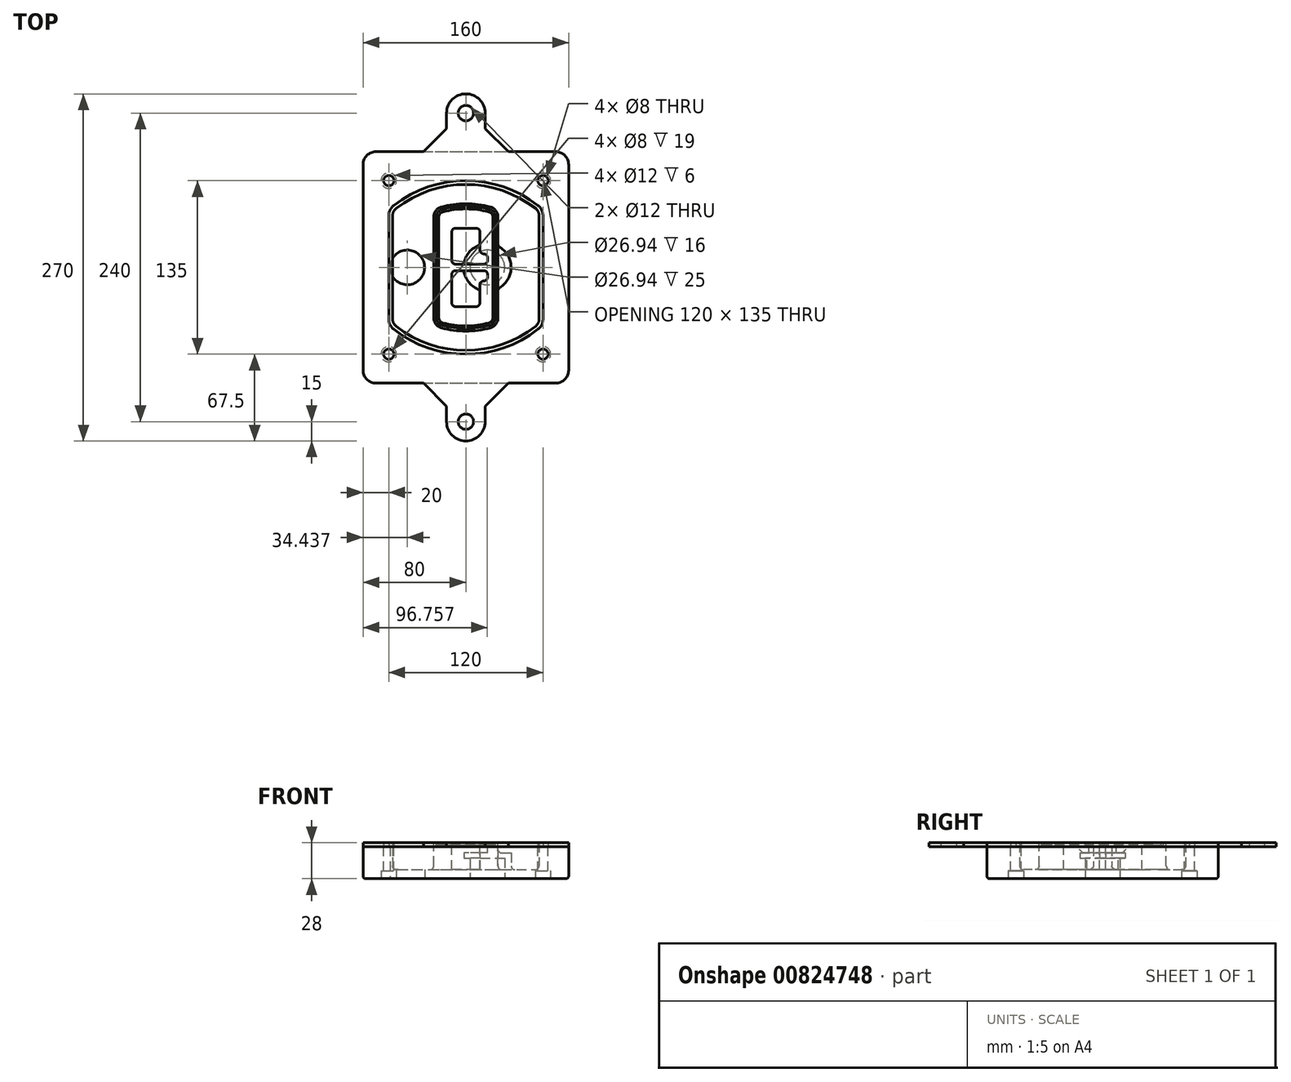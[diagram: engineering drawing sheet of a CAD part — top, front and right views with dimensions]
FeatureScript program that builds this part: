
annotation { "Feature Type Name" : "Feature", "Feature Type Description" : "" }
export const myFeature = defineFeature(function(context is Context, id is Id, definition is map)
    precondition{}
    {
        {
            var Q0;
            Q0=qCreatedBy(makeId("Top.planeOp"),FACE);
            var sketch = newSketch(context, id + "F0", { "sketchPlane" : qUnion([Q0])});
            skPoint(sketch, "E0.rect.middle", {"position": v(0, 0) * mm});
            skLineSegment(sketch, "E1.bottom", {"start": v(-70, -90) * mm, "end": v(70, -90) * mm});
            skLineSegment(sketch, "E1.top", {"start": v(-70, 90) * mm, "end": v(70, 90) * mm});
            skLineSegment(sketch, "E1.left", {"start": v(-80, -80) * mm, "end": v(-80, 80) * mm});
            skLineSegment(sketch, "E1.right", {"start": v(80, -80) * mm, "end": v(80, 80) * mm});
            skLineSegment(sketch, "E2", {"start": v(-80, 90) * mm, "end": v(80, -90) * mm, "construction": true});
            skLineSegment(sketch, "E3", {"start": v(80, 90) * mm, "end": v(-80, -90) * mm, "construction": true});
            skCircle(sketch, "E4", {"center": v(-60, 67.5) * mm, "radius": 4 * mm});
            skCircle(sketch, "E5", {"center": v(60, 67.5) * mm, "radius": 4 * mm});
            skCircle(sketch, "E6", {"center": v(60, -67.5) * mm, "radius": 4 * mm});
            skCircle(sketch, "E7", {"center": v(-60, -67.5) * mm, "radius": 4 * mm});
            skLineSegment(sketch, "E8", {"start": v(-60, 67.5) * mm, "end": v(60, 67.5) * mm, "construction": true});
            skLineSegment(sketch, "E9", {"start": v(60, 67.5) * mm, "end": v(60, -67.5) * mm, "construction": true});
            skLineSegment(sketch, "E10", {"start": v(60, -67.5) * mm, "end": v(-60, -67.5) * mm, "construction": true});
            skLineSegment(sketch, "E11", {"start": v(-60, -67.5) * mm, "end": v(-60, 67.5) * mm, "construction": true});
            skLineSegment(sketch, "E12", {"start": v(-60, 40.3) * mm, "end": v(-60, -40.3) * mm});
            skLineSegment(sketch, "E13", {"start": v(60, 40.3) * mm, "end": v(60, -40.3) * mm});
            skArc(sketch, "E14", {"start": v(56.15, 48.18) * mm, "mid": v(0, 67.5) * mm, "end": v(-56.15, 48.18) * mm});
            skArc(sketch, "E15", {"start": v(-56.15, -48.18) * mm, "mid": v(0, -67.5) * mm, "end": v(56.15, -48.18) * mm});
            skLineSegment(sketch, "E16", {"start": v(-60, 0) * mm, "end": v(60, 0) * mm, "construction": true});
            skPoint(sketch, "E17.visualSharp", {"position": v(-60, -45) * mm});
            skArc(sketch, "E17.filletArc", {"start": v(-60, -40.3) * mm, "mid": v(-58.99, -44.68) * mm, "end": v(-56.15, -48.18) * mm});
            skPoint(sketch, "E18.visualSharp", {"position": v(-60, 45) * mm});
            skArc(sketch, "E18.filletArc", {"start": v(-56.15, 48.18) * mm, "mid": v(-58.99, 44.68) * mm, "end": v(-60, 40.3) * mm});
            skPoint(sketch, "E19.visualSharp", {"position": v(60, 45) * mm});
            skArc(sketch, "E19.filletArc", {"start": v(60, 40.3) * mm, "mid": v(58.99, 44.68) * mm, "end": v(56.15, 48.18) * mm});
            skPoint(sketch, "E20.visualSharp", {"position": v(60, -45) * mm});
            skArc(sketch, "E20.filletArc", {"start": v(56.15, -48.18) * mm, "mid": v(58.99, -44.68) * mm, "end": v(60, -40.3) * mm});
            skPoint(sketch, "E21.visualSharp", {"position": v(-80, 90) * mm});
            skArc(sketch, "E21.filletArc", {"start": v(-70, 90) * mm, "mid": v(-77.07, 87.07) * mm, "end": v(-80, 80) * mm});
            skPoint(sketch, "E22.visualSharp", {"position": v(80, 90) * mm});
            skArc(sketch, "E22.filletArc", {"start": v(80, 80) * mm, "mid": v(77.07, 87.07) * mm, "end": v(70, 90) * mm});
            skPoint(sketch, "E23.visualSharp", {"position": v(80, -90) * mm});
            skArc(sketch, "E23.filletArc", {"start": v(70, -90) * mm, "mid": v(77.07, -87.07) * mm, "end": v(80, -80) * mm});
            skPoint(sketch, "E24.visualSharp", {"position": v(-80, -90) * mm});
            skArc(sketch, "E24.filletArc", {"start": v(-80, -80) * mm, "mid": v(-77.07, -87.07) * mm, "end": v(-70, -90) * mm});
            skArc(sketch, "E25.0", {"start": v(57, 40.3) * mm, "mid": v(56.3, 43.36) * mm, "end": v(54.3, 45.81) * mm});
            skLineSegment(sketch, "E25.1", {"start": v(57, 40.3) * mm, "end": v(57, -40.3) * mm});
            skArc(sketch, "E25.2", {"start": v(54.3, -45.81) * mm, "mid": v(56.3, -43.36) * mm, "end": v(57, -40.3) * mm});
            skArc(sketch, "E25.3", {"start": v(-54.3, -45.81) * mm, "mid": v(0, -64.5) * mm, "end": v(54.3, -45.81) * mm});
            skArc(sketch, "E25.4", {"start": v(-57, -40.3) * mm, "mid": v(-56.3, -43.36) * mm, "end": v(-54.3, -45.81) * mm});
            skArc(sketch, "E25.5", {"start": v(54.3, 45.81) * mm, "mid": v(0, 64.5) * mm, "end": v(-54.3, 45.81) * mm});
            skLineSegment(sketch, "E25.6", {"start": v(-57, 40.3) * mm, "end": v(-57, -40.3) * mm});
            skArc(sketch, "E25.7", {"start": v(-54.3, 45.81) * mm, "mid": v(-56.3, 43.36) * mm, "end": v(-57, 40.3) * mm});
            skArc(sketch, "E26.0", {"start": v(-58.62, 51.33) * mm, "mid": v(-62.58, 46.43) * mm, "end": v(-64, 40.3) * mm});
            skArc(sketch, "E26.1", {"start": v(58.62, 51.33) * mm, "mid": v(0, 71.5) * mm, "end": v(-58.62, 51.33) * mm});
            skArc(sketch, "E26.2", {"start": v(64, 40.3) * mm, "mid": v(62.58, 46.43) * mm, "end": v(58.62, 51.33) * mm});
            skLineSegment(sketch, "E26.3", {"start": v(64, 40.3) * mm, "end": v(64, -40.3) * mm});
            skArc(sketch, "E26.4", {"start": v(58.62, -51.33) * mm, "mid": v(62.58, -46.43) * mm, "end": v(64, -40.3) * mm});
            skLineSegment(sketch, "E26.5", {"start": v(-64, 40.3) * mm, "end": v(-64, -40.3) * mm});
            skArc(sketch, "E26.6", {"start": v(-58.62, -51.33) * mm, "mid": v(0, -71.5) * mm, "end": v(58.62, -51.33) * mm});
            skArc(sketch, "E26.7", {"start": v(-64, -40.3) * mm, "mid": v(-62.58, -46.43) * mm, "end": v(-58.62, -51.33) * mm});
            skSolve(sketch);
        }
        {
            var Q0;
            Q0=makeQuery(id+"F0.imprint","IMPRINT",FACE,{"disambiguationData":[TD([[makeQuery(id+"F0.imprint","IMPRINT",EDGE,{"derivedFrom":sQuery(id+"F0.wireOp",EDGE,"E1.bottom")}),1.0]])]});
            var Q1;
            Q1=makeQuery(id+"F0.imprint","IMPRINT",FACE,{"disambiguationData":[TD([[makeQuery(id+"F0.imprint","IMPRINT",EDGE,{"derivedFrom":sQuery(id+"F0.wireOp",EDGE,"E12")}),1.0]])]});
            var Q2;
            Q2=makeQuery(id+"F0.imprint","IMPRINT",FACE,{"disambiguationData":[TD([[makeQuery(id+"F0.imprint","IMPRINT",EDGE,{"derivedFrom":sQuery(id+"F0.wireOp",EDGE,"E25.0")}),1.0]])]});
            var Q3;
            Q3=makeQuery(id+"F0.imprint","IMPRINT",FACE,{"disambiguationData":[TD([[makeQuery(id+"F0.imprint","IMPRINT",EDGE,{"derivedFrom":sQuery(id+"F0.wireOp",EDGE,"E12")}),-1.0]])]});
            extrude(context, id + "F1", {"entities" : qUnion([Q0, Q1, Q2, Q3]), "oppositeDirection" : true, "depth" : 25 * mm});
        }
        {
            var Q0;
            Q0=makeQuery(id+"F0.imprint","IMPRINT",FACE,{"disambiguationData":[TD([[makeQuery(id+"F0.imprint","IMPRINT",EDGE,{"derivedFrom":sQuery(id+"F0.wireOp",EDGE,"E12")}),1.0]])]});
            extrude(context, id + "F2", {"entities" : qUnion([Q0]), "operationType" : NewBodyOperationType.ADD, "depth" : 3 * mm});
        }
        {
            var Q0;
            Q0=makeQuery(id+"F0.imprint","IMPRINT",FACE,{"disambiguationData":[TD([[makeQuery(id+"F0.imprint","IMPRINT",EDGE,{"derivedFrom":sQuery(id+"F0.wireOp",EDGE,"E25.0")}),1.0]])]});
            extrude(context, id + "F3", {"entities" : qUnion([Q0]), "operationType" : NewBodyOperationType.REMOVE, "oppositeDirection" : true, "depth" : 18 * mm});
        }
        {
            var Q0;
            Q0=makeQuery(id+"F2.opExtrude","CAP_FACE",FACE,{"disambiguationData":[OSD([sQuery(id+"F0.wireOp",EDGE,"E12"),sQuery(id+"F0.wireOp",EDGE,"E13"),sQuery(id+"F0.wireOp",EDGE,"E14"),sQuery(id+"F0.wireOp",EDGE,"E15"),sQuery(id+"F0.wireOp",EDGE,"E17.filletArc"),sQuery(id+"F0.wireOp",EDGE,"E18.filletArc"),sQuery(id+"F0.wireOp",EDGE,"E19.filletArc"),sQuery(id+"F0.wireOp",EDGE,"E20.filletArc"),sQuery(id+"F0.wireOp",EDGE,"E25.0"),sQuery(id+"F0.wireOp",EDGE,"E25.1"),sQuery(id+"F0.wireOp",EDGE,"E25.2"),sQuery(id+"F0.wireOp",EDGE,"E25.3"),sQuery(id+"F0.wireOp",EDGE,"E25.4"),sQuery(id+"F0.wireOp",EDGE,"E25.5"),sQuery(id+"F0.wireOp",EDGE,"E25.6"),sQuery(id+"F0.wireOp",EDGE,"E25.7")])],"isStart":false});
            var sketch = newSketch(context, id + "F4", { "sketchPlane" : qUnion([Q0])});
            skArc(sketch, "E27.0", {"start": v(-19.08, -46.97) * mm, "mid": v(0, -49.5) * mm, "end": v(19.08, -46.97) * mm});
            skArc(sketch, "E28.0", {"start": v(19.08, 46.97) * mm, "mid": v(0, 49.5) * mm, "end": v(-19.08, 46.97) * mm});
            skLineSegment(sketch, "E29", {"start": v(-25, 39.25) * mm, "end": v(-25, -39.25) * mm});
            skLineSegment(sketch, "E30", {"start": v(25, 39.25) * mm, "end": v(25, -39.25) * mm});
            skLineSegment(sketch, "E31", {"start": v(-25, 45.1) * mm, "end": v(25, 45.1) * mm, "construction": true});
            skLineSegment(sketch, "E32", {"start": v(-25, -45.1) * mm, "end": v(25, -45.1) * mm, "construction": true});
            skPoint(sketch, "E33.visualSharp", {"position": v(-25, 45.1) * mm});
            skArc(sketch, "E33.filletArc", {"start": v(-19.08, 46.97) * mm, "mid": v(-23.35, 44.11) * mm, "end": v(-25, 39.25) * mm});
            skPoint(sketch, "E34.visualSharp", {"position": v(25, 45.1) * mm});
            skArc(sketch, "E34.filletArc", {"start": v(25, 39.25) * mm, "mid": v(23.35, 44.11) * mm, "end": v(19.08, 46.97) * mm});
            skPoint(sketch, "E35.visualSharp", {"position": v(25, -45.1) * mm});
            skArc(sketch, "E35.filletArc", {"start": v(19.08, -46.97) * mm, "mid": v(23.35, -44.11) * mm, "end": v(25, -39.25) * mm});
            skPoint(sketch, "E36.visualSharp", {"position": v(-25, -45.1) * mm});
            skArc(sketch, "E36.filletArc", {"start": v(-25, -39.25) * mm, "mid": v(-23.35, -44.11) * mm, "end": v(-19.08, -46.97) * mm});
            skArc(sketch, "E37.0", {"start": v(54.3, 45.81) * mm, "mid": v(0, 64.5) * mm, "end": v(-54.3, 45.81) * mm});
            skArc(sketch, "E37.1", {"start": v(-54.3, 45.81) * mm, "mid": v(-56.3, 43.36) * mm, "end": v(-57, 40.3) * mm});
            skLineSegment(sketch, "E37.2", {"start": v(-57, 40.3) * mm, "end": v(-57, -40.3) * mm});
            skArc(sketch, "E37.3", {"start": v(-57, -40.3) * mm, "mid": v(-56.3, -43.36) * mm, "end": v(-54.3, -45.81) * mm});
            skArc(sketch, "E37.4", {"start": v(-54.3, -45.81) * mm, "mid": v(0, -64.5) * mm, "end": v(54.3, -45.81) * mm});
            skArc(sketch, "E37.5", {"start": v(54.3, -45.81) * mm, "mid": v(56.3, -43.36) * mm, "end": v(57, -40.3) * mm});
            skLineSegment(sketch, "E37.6", {"start": v(57, 40.3) * mm, "end": v(57, -40.3) * mm});
            skArc(sketch, "E37.7", {"start": v(57, 40.3) * mm, "mid": v(56.3, 43.36) * mm, "end": v(54.3, 45.81) * mm});
            skLineSegment(sketch, "E38.0", {"start": v(23, 39.25) * mm, "end": v(23, -39.25) * mm});
            skArc(sketch, "E38.1", {"start": v(18.56, -45.04) * mm, "mid": v(21.76, -42.9) * mm, "end": v(23, -39.25) * mm});
            skArc(sketch, "E38.2", {"start": v(-18.56, -45.04) * mm, "mid": v(0, -47.5) * mm, "end": v(18.56, -45.04) * mm});
            skArc(sketch, "E38.3", {"start": v(-23, -39.25) * mm, "mid": v(-21.76, -42.9) * mm, "end": v(-18.56, -45.04) * mm});
            skLineSegment(sketch, "E38.4", {"start": v(-23, 39.25) * mm, "end": v(-23, -39.25) * mm});
            skArc(sketch, "E38.5", {"start": v(23, 39.25) * mm, "mid": v(21.76, 42.9) * mm, "end": v(18.56, 45.04) * mm});
            skArc(sketch, "E38.6", {"start": v(-18.56, 45.04) * mm, "mid": v(-21.76, 42.9) * mm, "end": v(-23, 39.25) * mm});
            skArc(sketch, "E38.7", {"start": v(18.56, 45.04) * mm, "mid": v(0, 47.5) * mm, "end": v(-18.56, 45.04) * mm});
            skArc(sketch, "E39.0", {"start": v(21, 39.25) * mm, "mid": v(20.18, 41.68) * mm, "end": v(18.04, 43.1) * mm});
            skLineSegment(sketch, "E39.1", {"start": v(21, 39.25) * mm, "end": v(21, -39.25) * mm});
            skArc(sketch, "E39.2", {"start": v(18.04, -43.1) * mm, "mid": v(20.18, -41.68) * mm, "end": v(21, -39.25) * mm});
            skArc(sketch, "E39.3", {"start": v(-18.04, -43.1) * mm, "mid": v(0, -45.5) * mm, "end": v(18.04, -43.1) * mm});
            skArc(sketch, "E39.4", {"start": v(-21, -39.25) * mm, "mid": v(-20.18, -41.68) * mm, "end": v(-18.04, -43.1) * mm});
            skArc(sketch, "E39.5", {"start": v(18.04, 43.1) * mm, "mid": v(0, 45.5) * mm, "end": v(-18.04, 43.1) * mm});
            skLineSegment(sketch, "E39.6", {"start": v(-21, 39.25) * mm, "end": v(-21, -39.25) * mm});
            skArc(sketch, "E39.7", {"start": v(-18.04, 43.1) * mm, "mid": v(-20.18, 41.68) * mm, "end": v(-21, 39.25) * mm});
            skLineSegment(sketch, "E40", {"start": v(-25, 0) * mm, "end": v(25, 0) * mm, "construction": true});
            skLineSegment(sketch, "E41", {"start": v(-11, 5.5) * mm, "end": v(-11, 27.5) * mm});
            skLineSegment(sketch, "E42", {"start": v(-8, 30.5) * mm, "end": v(8, 30.5) * mm});
            skLineSegment(sketch, "E43", {"start": v(11, 27.5) * mm, "end": v(11, 13.5) * mm});
            skLineSegment(sketch, "E44", {"start": v(14, 10.5) * mm, "end": v(14, 10.5) * mm});
            skLineSegment(sketch, "E45", {"start": v(17, 7.5) * mm, "end": v(17, 5.5) * mm});
            skLineSegment(sketch, "E46", {"start": v(14, 2.5) * mm, "end": v(-8, 2.5) * mm});
            skPoint(sketch, "E47.visualSharp", {"position": v(-11, 30.5) * mm});
            skArc(sketch, "E47.filletArc", {"start": v(-8, 30.5) * mm, "mid": v(-10.12, 29.62) * mm, "end": v(-11, 27.5) * mm});
            skPoint(sketch, "E48.visualSharp", {"position": v(11, 30.5) * mm});
            skArc(sketch, "E48.filletArc", {"start": v(11, 27.5) * mm, "mid": v(10.12, 29.62) * mm, "end": v(8, 30.5) * mm});
            skPoint(sketch, "E49.visualSharp", {"position": v(11, 10.5) * mm});
            skArc(sketch, "E49.filletArc", {"start": v(11, 13.5) * mm, "mid": v(11.88, 11.38) * mm, "end": v(14, 10.5) * mm});
            skPoint(sketch, "E50.visualSharp", {"position": v(17, 10.5) * mm});
            skArc(sketch, "E50.filletArc", {"start": v(17, 7.5) * mm, "mid": v(16.12, 9.62) * mm, "end": v(14, 10.5) * mm});
            skPoint(sketch, "E51.visualSharp", {"position": v(17, 2.5) * mm});
            skArc(sketch, "E51.filletArc", {"start": v(14, 2.5) * mm, "mid": v(16.12, 3.38) * mm, "end": v(17, 5.5) * mm});
            skPoint(sketch, "E52.visualSharp", {"position": v(-11, 2.5) * mm});
            skArc(sketch, "E52.filletArc", {"start": v(-11, 5.5) * mm, "mid": v(-10.12, 3.38) * mm, "end": v(-8, 2.5) * mm});
            skLineSegment(sketch, "E53.0.MirrorCS", {"start": v(14, -2.5) * mm, "end": v(-8, -2.5) * mm});
            skArc(sketch, "E54.0.MirrorCS", {"start": v(-11, -5.5) * mm, "mid": v(-10.12, -3.38) * mm, "end": v(-8, -2.5) * mm});
            skLineSegment(sketch, "E55.0.MirrorCS", {"start": v(-11, -5.5) * mm, "end": v(-11, -27.5) * mm});
            skArc(sketch, "E56.0.MirrorCS", {"start": v(-8, -30.5) * mm, "mid": v(-10.12, -29.62) * mm, "end": v(-11, -27.5) * mm});
            skLineSegment(sketch, "E57.0.MirrorCS", {"start": v(-8, -30.5) * mm, "end": v(8, -30.5) * mm});
            skArc(sketch, "E58.0.MirrorCS", {"start": v(11, -27.5) * mm, "mid": v(10.12, -29.62) * mm, "end": v(8, -30.5) * mm});
            skLineSegment(sketch, "E59.0.MirrorCS", {"start": v(11, -27.5) * mm, "end": v(11, -13.5) * mm});
            skArc(sketch, "E60.0.MirrorCS", {"start": v(11, -13.5) * mm, "mid": v(11.88, -11.38) * mm, "end": v(14, -10.5) * mm});
            skArc(sketch, "E61.0.MirrorCS", {"start": v(17, -7.5) * mm, "mid": v(16.12, -9.62) * mm, "end": v(14, -10.5) * mm});
            skLineSegment(sketch, "E62.0.MirrorCS", {"start": v(17, -7.5) * mm, "end": v(17, -5.5) * mm});
            skArc(sketch, "E63.0.MirrorCS", {"start": v(14, -2.5) * mm, "mid": v(16.12, -3.38) * mm, "end": v(17, -5.5) * mm});
            skSolve(sketch);
        }
        {
            var Q0;
            Q0=makeQuery(id+"F4.imprint","IMPRINT",FACE,{"disambiguationData":[TD([[makeQuery(id+"F4.imprint","IMPRINT",EDGE,{"derivedFrom":sQuery(id+"F4.wireOp",EDGE,"E27.0")}),1.0]])]});
            var Q1;
            Q1=makeQuery(id+"F4.imprint","IMPRINT",FACE,{"disambiguationData":[TD([[makeQuery(id+"F4.imprint","IMPRINT",EDGE,{"derivedFrom":sQuery(id+"F4.wireOp",EDGE,"E38.0")}),-1.0]])]});
            var Q2;
            Q2=makeQuery(id+"F4.imprint","IMPRINT",FACE,{"disambiguationData":[TD([[makeQuery(id+"F4.imprint","IMPRINT",EDGE,{"derivedFrom":sQuery(id+"F4.wireOp",EDGE,"E39.0")}),1.0]])]});
            extrude(context, id + "F5", {"entities" : qUnion([Q0, Q1, Q2]), "operationType" : NewBodyOperationType.ADD, "endBound" : BoundingType.UP_TO_NEXT, "oppositeDirection" : true, "depth" : 25 * mm});
        }
        {
            var Q0;
            Q0=makeQuery(id+"F4.imprint","IMPRINT",FACE,{"disambiguationData":[TD([[makeQuery(id+"F4.imprint","IMPRINT",EDGE,{"derivedFrom":sQuery(id+"F4.wireOp",EDGE,"E38.0")}),-1.0]])]});
            extrude(context, id + "F6", {"entities" : qUnion([Q0]), "operationType" : NewBodyOperationType.REMOVE, "oppositeDirection" : true, "depth" : 2 * mm});
        }
        {
            var Q0;
            Q0=makeQuery(id+"F1.opExtrude","CAP_FACE",FACE,{"disambiguationData":[OSD([sQuery(id+"F0.wireOp",EDGE,"E1.bottom"),sQuery(id+"F0.wireOp",EDGE,"E1.top"),sQuery(id+"F0.wireOp",EDGE,"E1.left"),sQuery(id+"F0.wireOp",EDGE,"E1.right"),sQuery(id+"F0.wireOp",EDGE,"E4"),sQuery(id+"F0.wireOp",EDGE,"E5"),sQuery(id+"F0.wireOp",EDGE,"E6"),sQuery(id+"F0.wireOp",EDGE,"E7"),sQuery(id+"F0.wireOp",EDGE,"E21.filletArc"),sQuery(id+"F0.wireOp",EDGE,"E22.filletArc"),sQuery(id+"F0.wireOp",EDGE,"E23.filletArc"),sQuery(id+"F0.wireOp",EDGE,"E24.filletArc")])],"isStart":false});
            var sketch = newSketch(context, id + "F7", { "sketchPlane" : qUnion([Q0])});
            skCircle(sketch, "E64", {"center": v(16.76, 0) * mm, "radius": 13.47 * mm});
            skCircle(sketch, "E65", {"center": v(-45.56, 0) * mm, "radius": 13.47 * mm});
            skLineSegment(sketch, "E66", {"start": v(80, 0) * mm, "end": v(-80, 0) * mm});
            skCircle(sketch, "E67", {"center": v(16.76, 0) * mm, "radius": 18.47 * mm});
            skCircle(sketch, "E68", {"center": v(60, -67.5) * mm, "radius": 6 * mm});
            skCircle(sketch, "E69", {"center": v(-60, -67.5) * mm, "radius": 6 * mm});
            skCircle(sketch, "E70", {"center": v(-60, 67.5) * mm, "radius": 6 * mm});
            skCircle(sketch, "E71", {"center": v(60, 67.5) * mm, "radius": 6 * mm});
            skSolve(sketch);
        }
        {
            var Q0;
            {var subQ1=sQuery(id+"F7.wireOp",EDGE,"E66");var subQ4=sQuery(id+"F7.wireOp",EDGE,"E64");var subQ6=makeQuery(id+"F7.imprint","INTERSECT",VERTEX,{"disambiguationData":[OD(0.0)],"derivedFrom":[subQ4,subQ1]});Q0=makeQuery(id+"F7.imprint","IMPRINT",FACE,{"disambiguationData":[TD([[makeQuery(id+"F7.imprint","IMPRINT",EDGE,{"disambiguationData":[TD([[subQ6,-1.0]])],"derivedFrom":subQ4}),-1.0]])]});}
            var Q1;
            {var subQ0=sQuery(id+"F7.wireOp",EDGE,"E66");var subQ1=sQuery(id+"F7.wireOp",EDGE,"E64");var subQ3=makeQuery(id+"F7.imprint","INTERSECT",VERTEX,{"disambiguationData":[OD(0.0)],"derivedFrom":[subQ1,subQ0]});Q1=makeQuery(id+"F7.imprint","IMPRINT",FACE,{"disambiguationData":[TD([[makeQuery(id+"F7.imprint","IMPRINT",EDGE,{"disambiguationData":[TD([[subQ3,-1.0]])],"derivedFrom":subQ1}),1.0]])]});}
            var Q2;
            {var subQ0=sQuery(id+"F7.wireOp",EDGE,"E66");var subQ1=sQuery(id+"F7.wireOp",EDGE,"E64");var subQ3=makeQuery(id+"F7.imprint","INTERSECT",VERTEX,{"disambiguationData":[OD(0.0)],"derivedFrom":[subQ1,subQ0]});Q2=makeQuery(id+"F7.imprint","IMPRINT",FACE,{"disambiguationData":[TD([[makeQuery(id+"F7.imprint","IMPRINT",EDGE,{"disambiguationData":[TD([[subQ3,1.0]])],"derivedFrom":subQ1}),1.0]])]});}
            var Q3;
            {var subQ1=sQuery(id+"F7.wireOp",EDGE,"E66");var subQ4=sQuery(id+"F7.wireOp",EDGE,"E64");var subQ6=makeQuery(id+"F7.imprint","INTERSECT",VERTEX,{"disambiguationData":[OD(0.0)],"derivedFrom":[subQ4,subQ1]});Q3=makeQuery(id+"F7.imprint","IMPRINT",FACE,{"disambiguationData":[TD([[makeQuery(id+"F7.imprint","IMPRINT",EDGE,{"disambiguationData":[TD([[subQ6,1.0]])],"derivedFrom":subQ4}),-1.0]])]});}
            extrude(context, id + "F8", {"entities" : qUnion([Q0, Q1, Q2, Q3]), "operationType" : NewBodyOperationType.ADD, "oppositeDirection" : true, "depth" : 20 * mm});
        }
        {
            var Q0;
            {var subQ0=sQuery(id+"F7.wireOp",EDGE,"E66");var subQ1=sQuery(id+"F7.wireOp",EDGE,"E64");var subQ3=makeQuery(id+"F7.imprint","INTERSECT",VERTEX,{"disambiguationData":[OD(0.0)],"derivedFrom":[subQ1,subQ0]});Q0=makeQuery(id+"F7.imprint","IMPRINT",FACE,{"disambiguationData":[TD([[makeQuery(id+"F7.imprint","IMPRINT",EDGE,{"disambiguationData":[TD([[subQ3,-1.0]])],"derivedFrom":subQ1}),1.0]])]});}
            var Q1;
            {var subQ0=sQuery(id+"F7.wireOp",EDGE,"E66");var subQ1=sQuery(id+"F7.wireOp",EDGE,"E64");var subQ3=makeQuery(id+"F7.imprint","INTERSECT",VERTEX,{"disambiguationData":[OD(0.0)],"derivedFrom":[subQ1,subQ0]});Q1=makeQuery(id+"F7.imprint","IMPRINT",FACE,{"disambiguationData":[TD([[makeQuery(id+"F7.imprint","IMPRINT",EDGE,{"disambiguationData":[TD([[subQ3,1.0]])],"derivedFrom":subQ1}),1.0]])]});}
            extrude(context, id + "F9", {"entities" : qUnion([Q0, Q1]), "operationType" : NewBodyOperationType.REMOVE, "oppositeDirection" : true, "depth" : 16 * mm});
        }
        {
            var Q0;
            {var subQ0=sQuery(id+"F7.wireOp",EDGE,"E66");var subQ1=sQuery(id+"F7.wireOp",EDGE,"E65");var subQ3=makeQuery(id+"F7.imprint","INTERSECT",VERTEX,{"disambiguationData":[OD(0.0)],"derivedFrom":[subQ1,subQ0]});Q0=makeQuery(id+"F7.imprint","IMPRINT",FACE,{"disambiguationData":[TD([[makeQuery(id+"F7.imprint","IMPRINT",EDGE,{"disambiguationData":[TD([[subQ3,-1.0]])],"derivedFrom":subQ1}),1.0]])]});}
            var Q1;
            {var subQ0=sQuery(id+"F7.wireOp",EDGE,"E66");var subQ1=sQuery(id+"F7.wireOp",EDGE,"E65");var subQ3=makeQuery(id+"F7.imprint","INTERSECT",VERTEX,{"disambiguationData":[OD(0.0)],"derivedFrom":[subQ1,subQ0]});Q1=makeQuery(id+"F7.imprint","IMPRINT",FACE,{"disambiguationData":[TD([[makeQuery(id+"F7.imprint","IMPRINT",EDGE,{"disambiguationData":[TD([[subQ3,1.0]])],"derivedFrom":subQ1}),1.0]])]});}
            extrude(context, id + "F10", {"entities" : qUnion([Q0, Q1]), "operationType" : NewBodyOperationType.REMOVE, "oppositeDirection" : true, "depth" : 25 * mm});
        }
        {
            var Q0;
            Q0=makeQuery(id+"F7.imprint","IMPRINT",FACE,{"disambiguationData":[TD([[makeQuery(id+"F7.imprint","IMPRINT",EDGE,{"derivedFrom":sQuery(id+"F7.wireOp",EDGE,"E68")}),1.0]])]});
            var Q1;
            Q1=makeQuery(id+"F7.imprint","IMPRINT",FACE,{"disambiguationData":[TD([[makeQuery(id+"F7.imprint","IMPRINT",EDGE,{"derivedFrom":makeQuery(id+"F1.opExtrude","CAP_EDGE",EDGE,{"disambiguationData":[OSD([sQuery(id+"F0.wireOp",EDGE,"E5")])],"isStart":false})}),-1.0]])]});
            var Q2;
            Q2=makeQuery(id+"F7.imprint","IMPRINT",FACE,{"disambiguationData":[TD([[makeQuery(id+"F7.imprint","IMPRINT",EDGE,{"derivedFrom":sQuery(id+"F7.wireOp",EDGE,"E69")}),1.0]])]});
            var Q3;
            Q3=makeQuery(id+"F7.imprint","IMPRINT",FACE,{"disambiguationData":[TD([[makeQuery(id+"F7.imprint","IMPRINT",EDGE,{"derivedFrom":makeQuery(id+"F1.opExtrude","CAP_EDGE",EDGE,{"disambiguationData":[OSD([sQuery(id+"F0.wireOp",EDGE,"E4")])],"isStart":false})}),-1.0]])]});
            var Q4;
            Q4=makeQuery(id+"F7.imprint","IMPRINT",FACE,{"disambiguationData":[TD([[makeQuery(id+"F7.imprint","IMPRINT",EDGE,{"derivedFrom":sQuery(id+"F7.wireOp",EDGE,"E70")}),1.0]])]});
            var Q5;
            Q5=makeQuery(id+"F7.imprint","IMPRINT",FACE,{"disambiguationData":[TD([[makeQuery(id+"F7.imprint","IMPRINT",EDGE,{"derivedFrom":makeQuery(id+"F1.opExtrude","CAP_EDGE",EDGE,{"disambiguationData":[OSD([sQuery(id+"F0.wireOp",EDGE,"E7")])],"isStart":false})}),-1.0]])]});
            var Q6;
            Q6=makeQuery(id+"F7.imprint","IMPRINT",FACE,{"disambiguationData":[TD([[makeQuery(id+"F7.imprint","IMPRINT",EDGE,{"derivedFrom":sQuery(id+"F7.wireOp",EDGE,"E71")}),1.0]])]});
            var Q7;
            Q7=makeQuery(id+"F7.imprint","IMPRINT",FACE,{"disambiguationData":[TD([[makeQuery(id+"F7.imprint","IMPRINT",EDGE,{"derivedFrom":makeQuery(id+"F1.opExtrude","CAP_EDGE",EDGE,{"disambiguationData":[OSD([sQuery(id+"F0.wireOp",EDGE,"E6")])],"isStart":false})}),-1.0]])]});
            extrude(context, id + "F11", {"entities" : qUnion([Q0, Q1, Q2, Q3, Q4, Q5, Q6, Q7]), "operationType" : NewBodyOperationType.REMOVE, "oppositeDirection" : true, "depth" : 6 * mm});
        }
        {
            var Q0;
            Q0=makeQuery(id+"F9.boolean.opBoolean","COPY",FACE,{"derivedFrom":makeQuery(id+"F9.opExtrude","CAP_FACE",FACE,{"disambiguationData":[OSD([sQuery(id+"F7.wireOp",EDGE,"E64")])],"isStart":false})});
            var sketch = newSketch(context, id + "F12", { "sketchPlane" : qUnion([Q0])});
            skArc(sketch, "E72.0", {"start": v(11, 17.55) * mm, "mid": v(2.57, 11.82) * mm, "end": v(-1.54, 2.5) * mm});
            skArc(sketch, "E72.1", {"start": v(-1.54, -2.5) * mm, "mid": v(2.57, -11.82) * mm, "end": v(11, -17.55) * mm});
            skLineSegment(sketch, "E73", {"start": v(-1.54, -2.5) * mm, "end": v(14, -2.5) * mm});
            skLineSegment(sketch, "E74.0", {"start": v(14, 2.5) * mm, "end": v(-1.54, 2.5) * mm});
            skArc(sketch, "E74.1", {"start": v(14, 2.5) * mm, "mid": v(16.12, 3.38) * mm, "end": v(17, 5.5) * mm});
            skLineSegment(sketch, "E74.2", {"start": v(17, 7.5) * mm, "end": v(17, 5.5) * mm});
            skArc(sketch, "E74.3", {"start": v(17, 7.5) * mm, "mid": v(16.12, 9.62) * mm, "end": v(14, 10.5) * mm});
            skArc(sketch, "E74.4", {"start": v(11, 13.5) * mm, "mid": v(11.88, 11.38) * mm, "end": v(14, 10.5) * mm});
            skLineSegment(sketch, "E74.5", {"start": v(11, 17.55) * mm, "end": v(11, 13.5) * mm});
            skLineSegment(sketch, "E74.7", {"start": v(14, -2.5) * mm, "end": v(-1.54, -2.5) * mm});
            skArc(sketch, "E74.8", {"start": v(14, -2.5) * mm, "mid": v(16.12, -3.38) * mm, "end": v(17, -5.5) * mm});
            skLineSegment(sketch, "E74.9", {"start": v(17, -7.5) * mm, "end": v(17, -5.5) * mm});
            skArc(sketch, "E74.10", {"start": v(17, -7.5) * mm, "mid": v(16.12, -9.62) * mm, "end": v(14, -10.5) * mm});
            skArc(sketch, "E74.11", {"start": v(11, -13.5) * mm, "mid": v(11.88, -11.38) * mm, "end": v(14, -10.5) * mm});
            skLineSegment(sketch, "E74.12", {"start": v(11, -17.55) * mm, "end": v(11, -13.5) * mm});
            skPoint(sketch, "E75.orphan", {"position": v(11, -27.5) * mm});
            skPoint(sketch, "E76.orphan", {"position": v(-8, -2.5) * mm});
            skPoint(sketch, "E77.orphan", {"position": v(-8, 2.5) * mm});
            skPoint(sketch, "E78.orphan", {"position": v(11, 27.5) * mm});
            skSolve(sketch);
        }
        {
            var Q0;
            {var subQ7=sQuery(id+"F12.wireOp",EDGE,"E72.0");var subQ14=sQuery(id+"F12.wireOp",EDGE,"E72.1");var subQ16=sQuery(id+"F12.wireOp",EDGE,"E74.1");var subQ18=sQuery(id+"F12.wireOp",EDGE,"E74.8");Q0=qUnion([makeQuery(id+"F12.imprint","IMPRINT",FACE,{"disambiguationData":[TD([[makeQuery(id+"F12.imprint","IMPRINT",EDGE,{"derivedFrom":subQ7}),1.0]])]}),makeQuery(id+"F12.imprint","IMPRINT",FACE,{"disambiguationData":[TD([[makeQuery(id+"F12.imprint","IMPRINT",EDGE,{"derivedFrom":subQ14}),1.0]])]}),makeQuery(id+"F12.imprint","IMPRINT",FACE,{"disambiguationData":[TD([[makeQuery(id+"F12.imprint","IMPRINT",EDGE,{"derivedFrom":subQ16}),1.0]])]}),makeQuery(id+"F12.imprint","IMPRINT",FACE,{"disambiguationData":[TD([[makeQuery(id+"F12.imprint","IMPRINT",EDGE,{"derivedFrom":subQ18}),-1.0]])]})]);}
            var Q1;
            Q1=makeQuery(id+"F5.boolean.opBoolean","SPLIT",FACE,{"disambiguationData":[TD([makeQuery(id+"F5.opExtrude","SWEPT_FACE",FACE,{"disambiguationData":[OSD([sQuery(id+"F4.wireOp",EDGE,"E41")])]})])],"derivedFrom":makeQuery(id+"F3.boolean.opBoolean","COPY",FACE,{"derivedFrom":makeQuery(id+"F3.opExtrude","CAP_FACE",FACE,{"disambiguationData":[OSD([sQuery(id+"F0.wireOp",EDGE,"E25.0"),sQuery(id+"F0.wireOp",EDGE,"E25.1"),sQuery(id+"F0.wireOp",EDGE,"E25.2"),sQuery(id+"F0.wireOp",EDGE,"E25.3"),sQuery(id+"F0.wireOp",EDGE,"E25.4"),sQuery(id+"F0.wireOp",EDGE,"E25.5"),sQuery(id+"F0.wireOp",EDGE,"E25.6"),sQuery(id+"F0.wireOp",EDGE,"E25.7")])],"isStart":false})})});
            extrude(context, id + "F13", {"entities" : qUnion([Q0]), "operationType" : NewBodyOperationType.REMOVE, "endBound" : BoundingType.UP_TO_SURFACE, "endBoundEntityFace" : qUnion([Q1]), "depth" : 25 * mm});
        }
        {
            var Q0;
            Q0=makeQuery(id+"F3.boolean.opBoolean","COPY",EDGE,{"derivedFrom":makeQuery(id+"F3.opExtrude","CAP_EDGE",EDGE,{"disambiguationData":[OSD([sQuery(id+"F0.wireOp",EDGE,"E25.6")])],"isStart":false})});
            var Q1;
            Q1=makeQuery(id+"F8.boolean.opBoolean","INTERSECT",EDGE,{"derivedFrom":[makeQuery(id+"F5.opExtrude","SWEPT_FACE",FACE,{"disambiguationData":[OSD([sQuery(id+"F4.wireOp",EDGE,"E30")])]}),makeQuery(id+"F8.opExtrude","CAP_FACE",FACE,{"disambiguationData":[OSD([sQuery(id+"F7.wireOp",EDGE,"E67")])],"isStart":false})]});
            var Q2;
            Q2=makeQuery(id+"F8.boolean.opBoolean","INTERSECT",EDGE,{"disambiguationData":[OD(1.0)],"derivedFrom":[makeQuery(id+"F5.opExtrude","SWEPT_FACE",FACE,{"disambiguationData":[OSD([sQuery(id+"F4.wireOp",EDGE,"E30")])]}),makeQuery(id+"F8.opExtrude","SWEPT_FACE",FACE,{"disambiguationData":[OSD([sQuery(id+"F7.wireOp",EDGE,"E67")])]})]});
            var Q3;
            {var subQ0=sQuery(id+"F4.wireOp",EDGE,"E30");Q3=makeQuery(id+"F8.boolean.opBoolean","SPLIT",EDGE,{"disambiguationData":[TD([makeQuery(id+"F5.opExtrude","SWEPT_FACE",FACE,{"disambiguationData":[OSD([sQuery(id+"F4.wireOp",EDGE,"E35.filletArc")])]})])],"derivedFrom":makeQuery(id+"F5.opExtrude","CAP_EDGE",EDGE,{"disambiguationData":[OSD([subQ0])],"isStart":false})});}
            var Q4;
            {var subQ0=sQuery(id+"F0.wireOp",EDGE,"E25.7");var subQ1=sQuery(id+"F0.wireOp",EDGE,"E25.1");var subQ2=sQuery(id+"F0.wireOp",EDGE,"E25.6");var subQ3=sQuery(id+"F0.wireOp",EDGE,"E25.5");var subQ4=sQuery(id+"F0.wireOp",EDGE,"E25.4");var subQ5=sQuery(id+"F0.wireOp",EDGE,"E25.0");var subQ6=sQuery(id+"F0.wireOp",EDGE,"E25.2");var subQ7=sQuery(id+"F0.wireOp",EDGE,"E25.3");Q4=makeQuery(id+"F8.boolean.opBoolean","INTERSECT",EDGE,{"derivedFrom":[makeQuery(id+"F5.boolean.opBoolean","SPLIT",FACE,{"disambiguationData":[TD([makeQuery(id+"F2.opExtrude","SWEPT_FACE",FACE,{"disambiguationData":[OSD([subQ5])]})])],"derivedFrom":makeQuery(id+"F3.boolean.opBoolean","COPY",FACE,{"derivedFrom":makeQuery(id+"F3.opExtrude","CAP_FACE",FACE,{"disambiguationData":[OSD([subQ5,subQ1,subQ6,subQ7,subQ4,subQ3,subQ2,subQ0])],"isStart":false})})}),makeQuery(id+"F8.opExtrude","SWEPT_FACE",FACE,{"disambiguationData":[OSD([sQuery(id+"F7.wireOp",EDGE,"E67")])]})]});}
            var Q5;
            Q5=makeQuery(id+"F8.boolean.opBoolean","INTERSECT",EDGE,{"disambiguationData":[OD(0.0)],"derivedFrom":[makeQuery(id+"F5.opExtrude","SWEPT_FACE",FACE,{"disambiguationData":[OSD([sQuery(id+"F4.wireOp",EDGE,"E30")])]}),makeQuery(id+"F8.opExtrude","SWEPT_FACE",FACE,{"disambiguationData":[OSD([sQuery(id+"F7.wireOp",EDGE,"E67")])]})]});
            fillet(context, id + "F14", {"entities" : qUnion([Q0, Q1, Q2, Q3, Q4, Q5]), "radius" : 3 * mm, "tangentPropagation" : true, "allowEdgeOverflow" : false});
        }
        {
            var Q0;
            Q0=makeQuery(id+"F1.opExtrude","CAP_EDGE",EDGE,{"disambiguationData":[OSD([sQuery(id+"F0.wireOp",EDGE,"E1.bottom")])],"isStart":false});
            fillet(context, id + "F15", {"entities" : qUnion([Q0]), "radius" : 2 * mm, "tangentPropagation" : true, "allowEdgeOverflow" : false});
        }
        {
            var Q0;
            {var subQ0=sQuery(id+"F0.wireOp",EDGE,"E21.filletArc");var subQ1=sQuery(id+"F0.wireOp",EDGE,"E7");var subQ2=sQuery(id+"F0.wireOp",EDGE,"E6");var subQ3=sQuery(id+"F0.wireOp",EDGE,"E5");var subQ4=sQuery(id+"F0.wireOp",EDGE,"E4");var subQ5=sQuery(id+"F0.wireOp",EDGE,"E22.filletArc");var subQ6=sQuery(id+"F0.wireOp",EDGE,"E1.bottom");var subQ7=sQuery(id+"F0.wireOp",EDGE,"E1.right");var subQ8=sQuery(id+"F0.wireOp",EDGE,"E1.top");var subQ9=sQuery(id+"F0.wireOp",EDGE,"E1.left");var subQ10=sQuery(id+"F0.wireOp",EDGE,"E23.filletArc");var subQ11=sQuery(id+"F0.wireOp",EDGE,"E24.filletArc");Q0=makeQuery(id+"F2.boolean.opBoolean","SPLIT",FACE,{"disambiguationData":[TD([makeQuery(id+"F1.opExtrude","SWEPT_FACE",FACE,{"disambiguationData":[OSD([subQ6])]})])],"derivedFrom":makeQuery(id+"F1.opExtrude","CAP_FACE",FACE,{"disambiguationData":[OSD([subQ6,subQ8,subQ9,subQ7,subQ4,subQ3,subQ2,subQ1,subQ0,subQ5,subQ10,subQ11])],"isStart":true})});}
            var sketch = newSketch(context, id + "F16", { "sketchPlane" : qUnion([Q0])});
            skLineSegment(sketch, "E79", {"start": v(0, 90) * mm, "end": v(0, 120) * mm, "construction": true});
            skCircle(sketch, "E80", {"center": v(0, 120) * mm, "radius": 6 * mm});
            skLineSegment(sketch, "E81", {"start": v(-33, 90) * mm, "end": v(-15, 108) * mm});
            skLineSegment(sketch, "E82", {"start": v(33, 90) * mm, "end": v(15, 108) * mm});
            skLineSegment(sketch, "E83", {"start": v(-15, 108) * mm, "end": v(-15, 120) * mm});
            skLineSegment(sketch, "E84", {"start": v(15, 108) * mm, "end": v(15, 120) * mm});
            skArc(sketch, "E85", {"start": v(15, 120) * mm, "mid": v(0, 135) * mm, "end": v(-15, 120) * mm});
            skLineSegment(sketch, "E86", {"start": v(-80, 0) * mm, "end": v(80, 0) * mm, "construction": true});
            skLineSegment(sketch, "E87.MirrorCS", {"start": v(-33, -90) * mm, "end": v(-15, -108) * mm});
            skLineSegment(sketch, "E88.MirrorCS", {"start": v(-15, -108) * mm, "end": v(-15, -120) * mm});
            skArc(sketch, "E89.MirrorCS", {"start": v(15, -120) * mm, "mid": v(0, -135) * mm, "end": v(-15, -120) * mm});
            skLineSegment(sketch, "E90.MirrorCS", {"start": v(15, -108) * mm, "end": v(15, -120) * mm});
            skLineSegment(sketch, "E91.MirrorCS", {"start": v(33, -90) * mm, "end": v(15, -108) * mm});
            skCircle(sketch, "E92.MirrorC", {"center": v(0, -120) * mm, "radius": 6 * mm});
            skLineSegment(sketch, "E93.MirrorCS", {"start": v(0, -90) * mm, "end": v(0, -120) * mm, "construction": true});
            skSolve(sketch);
        }
        {
            var Q0;
            Q0=makeQuery(id+"F16.imprint","IMPRINT",FACE,{"disambiguationData":[TD([[makeQuery(id+"F16.imprint","IMPRINT",EDGE,{"derivedFrom":sQuery(id+"F16.wireOp",EDGE,"E80")}),-1.0]])]});
            var Q1;
            Q1=makeQuery(id+"F16.imprint","IMPRINT",FACE,{"disambiguationData":[TD([[makeQuery(id+"F16.imprint","IMPRINT",EDGE,{"derivedFrom":makeQuery(id+"F1.opExtrude","CAP_EDGE",EDGE,{"disambiguationData":[OSD([sQuery(id+"F0.wireOp",EDGE,"E1.left")])],"isStart":true})}),-1.0]])]});
            var Q2;
            {var subQ0=sQuery(id+"F16.wireOp",EDGE,"E87.MirrorCS");Q2=makeQuery(id+"F16.imprint","IMPRINT",FACE,{"disambiguationData":[TD([[makeQuery(id+"F16.imprint","IMPRINT",EDGE,{"derivedFrom":subQ0}),1.0]])]});}
            var Q3;
            Q3=makeQuery(id+"F2.opExtrude","CAP_FACE",FACE,{"disambiguationData":[OSD([sQuery(id+"F0.wireOp",EDGE,"E12"),sQuery(id+"F0.wireOp",EDGE,"E13"),sQuery(id+"F0.wireOp",EDGE,"E14"),sQuery(id+"F0.wireOp",EDGE,"E15"),sQuery(id+"F0.wireOp",EDGE,"E17.filletArc"),sQuery(id+"F0.wireOp",EDGE,"E18.filletArc"),sQuery(id+"F0.wireOp",EDGE,"E19.filletArc"),sQuery(id+"F0.wireOp",EDGE,"E20.filletArc"),sQuery(id+"F0.wireOp",EDGE,"E25.0"),sQuery(id+"F0.wireOp",EDGE,"E25.1"),sQuery(id+"F0.wireOp",EDGE,"E25.2"),sQuery(id+"F0.wireOp",EDGE,"E25.3"),sQuery(id+"F0.wireOp",EDGE,"E25.4"),sQuery(id+"F0.wireOp",EDGE,"E25.5"),sQuery(id+"F0.wireOp",EDGE,"E25.6"),sQuery(id+"F0.wireOp",EDGE,"E25.7")])],"isStart":false});
            extrude(context, id + "F17", {"entities" : qUnion([Q0, Q1, Q2]), "endBound" : BoundingType.UP_TO_SURFACE, "depth" : 25 * mm, "endBoundEntityFace" : qUnion([Q3]), "offsetDistance" : 25 * mm});
        }
    });
